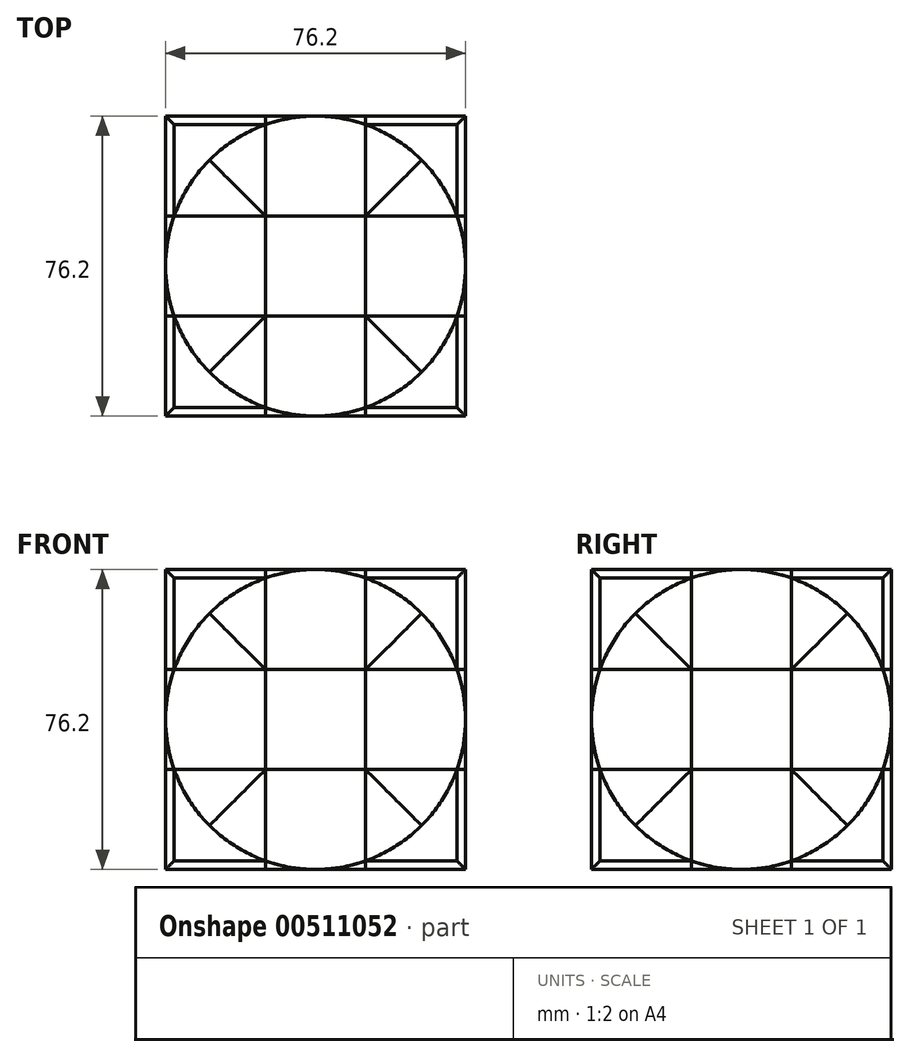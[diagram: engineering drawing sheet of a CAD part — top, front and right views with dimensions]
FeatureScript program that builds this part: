
annotation { "Feature Type Name" : "Feature", "Feature Type Description" : "" }
export const myFeature = defineFeature(function(context is Context, id is Id, definition is map)
    precondition{}
    {
        {
            var Q0;
            Q0=qCreatedBy(makeId("Front.planeOp"),FACE);
            var sketch = newSketch(context, id + "F0", { "sketchPlane" : qUnion([Q0])});
            skLineSegment(sketch, "E0.bottom", {"start": v(-38.1, 38.1) * mm, "end": v(38.1, 38.1) * mm});
            skLineSegment(sketch, "E0.top", {"start": v(-38.1, -38.1) * mm, "end": v(38.1, -38.1) * mm});
            skLineSegment(sketch, "E0.left", {"start": v(-38.1, 38.1) * mm, "end": v(-38.1, -38.1) * mm});
            skLineSegment(sketch, "E0.right", {"start": v(38.1, 38.1) * mm, "end": v(38.1, -38.1) * mm});
            skPoint(sketch, "E0.middle", {"position": v(0, 0) * mm});
            skSolve(sketch);
        }
        {
            var Q0;
            Q0=makeQuery(id+"F0.imprint","IMPRINT",FACE,{"disambiguationData":[TD([[makeQuery(id+"F0.imprint","IMPRINT",EDGE,{"derivedFrom":sQuery(id+"F0.wireOp",EDGE,"E0.bottom")}),-1.0]])]});
            extrude(context, id + "F1", {"entities" : qUnion([Q0]), "depth" : 76.2 * mm});
        }
        {
            var Q0;
            Q0=makeQuery(id+"F1.opExtrude","CAP_FACE",FACE,{"disambiguationData":[OSD([sQuery(id+"F0.wireOp",EDGE,"E0.bottom"),sQuery(id+"F0.wireOp",EDGE,"E0.top"),sQuery(id+"F0.wireOp",EDGE,"E0.left"),sQuery(id+"F0.wireOp",EDGE,"E0.right")])],"isStart":false});
            var sketch = newSketch(context, id + "F2", { "sketchPlane" : qUnion([Q0])});
            skCircle(sketch, "E1", {"center": v(0, 0) * mm, "radius": 38.1 * mm});
            skPoint(sketch, "E1.first.point", {"position": v(0, 38.1) * mm});
            skPoint(sketch, "E1.second.point", {"position": v(-38.1, 0) * mm});
            skPoint(sketch, "E1.third.point", {"position": v(0, -38.1) * mm});
            skSolve(sketch);
        }
        {
            var Q0;
            Q0=makeQuery(id+"F1.opExtrude","SWEPT_FACE",FACE,{"disambiguationData":[OSD([sQuery(id+"F0.wireOp",EDGE,"E0.right")])]});
            var sketch = newSketch(context, id + "F3", { "sketchPlane" : qUnion([Q0])});
            skCircle(sketch, "E2", {"center": v(-38.1, 0) * mm, "radius": 38.1 * mm});
            skPoint(sketch, "E2.first.point", {"position": v(-38.1, 38.1) * mm});
            skPoint(sketch, "E2.second.point", {"position": v(-76.2, 0) * mm});
            skPoint(sketch, "E2.third.point", {"position": v(-38.1, -38.1) * mm});
            skSolve(sketch);
        }
        {
            var Q0;
            {var subQ0=sQuery(id+"F2.wireOp",EDGE,"E1");var subQ1=makeQuery(id+"F2.imprint","INTERSECT",VERTEX,{"derivedFrom":[makeQuery(id+"F1.opExtrude","CAP_EDGE",EDGE,{"disambiguationData":[OSD([sQuery(id+"F0.wireOp",EDGE,"E0.bottom")])],"isStart":false}),subQ0]});Q0=makeQuery(id+"F2.imprint","IMPRINT",FACE,{"disambiguationData":[TD([[makeQuery(id+"F2.imprint","IMPRINT",EDGE,{"disambiguationData":[TD([[subQ1,1.0]])],"derivedFrom":subQ0}),1.0]])]});}
            extrude(context, id + "F4", {"entities" : qUnion([Q0]), "operationType" : NewBodyOperationType.ADD, "oppositeDirection" : true, "depth" : 76.2 * mm, "offsetDistance" : 25.4 * mm});
        }
        {
            var Q0;
            {var subQ0=sQuery(id+"F3.wireOp",EDGE,"E2");var subQ1=sQuery(id+"F0.wireOp",EDGE,"E0.right");var subQ3=makeQuery(id+"F3.imprint","INTERSECT",VERTEX,{"derivedFrom":[makeQuery(id+"F1.opExtrude","CAP_EDGE",EDGE,{"disambiguationData":[OSD([subQ1])],"isStart":true}),subQ0]});Q0=makeQuery(id+"F3.imprint","IMPRINT",FACE,{"disambiguationData":[TD([[makeQuery(id+"F3.imprint","IMPRINT",EDGE,{"disambiguationData":[TD([[subQ3,-1.0]])],"derivedFrom":subQ0}),1.0]])]});}
            extrude(context, id + "F5", {"entities" : qUnion([Q0]), "operationType" : NewBodyOperationType.ADD, "oppositeDirection" : true, "depth" : 76.2 * mm, "offsetDistance" : 25.4 * mm});
        }
        {
            var Q0;
            Q0=makeQuery(id+"F1.opExtrude","SWEPT_FACE",FACE,{"disambiguationData":[OSD([sQuery(id+"F0.wireOp",EDGE,"E0.left")])]});
            var sketch = newSketch(context, id + "F6", { "sketchPlane" : qUnion([Q0])});
            skCircle(sketch, "E3", {"center": v(38.1, 0) * mm, "radius": 38.1 * mm});
            skPoint(sketch, "E3.first.point", {"position": v(38.1, 38.1) * mm});
            skPoint(sketch, "E3.second.point", {"position": v(0, 0) * mm});
            skPoint(sketch, "E3.third.point", {"position": v(38.1, -38.1) * mm});
            skSolve(sketch);
        }
        {
            var Q0;
            Q0=makeQuery(id+"F1.opExtrude","CAP_FACE",FACE,{"disambiguationData":[OSD([sQuery(id+"F0.wireOp",EDGE,"E0.bottom"),sQuery(id+"F0.wireOp",EDGE,"E0.top"),sQuery(id+"F0.wireOp",EDGE,"E0.left"),sQuery(id+"F0.wireOp",EDGE,"E0.right")])],"isStart":true});
            var sketch = newSketch(context, id + "F7", { "sketchPlane" : qUnion([Q0])});
            skCircle(sketch, "E4", {"center": v(0, 0) * mm, "radius": 38.1 * mm});
            skPoint(sketch, "E4.first.point", {"position": v(0, 38.1) * mm});
            skPoint(sketch, "E4.second.point", {"position": v(-38.1, 0) * mm});
            skPoint(sketch, "E4.third.point", {"position": v(0, -38.1) * mm});
            skSolve(sketch);
        }
        {
            var Q0;
            {var subQ0=sQuery(id+"F7.wireOp",EDGE,"E4");var subQ1=makeQuery(id+"F7.imprint","INTERSECT",VERTEX,{"derivedFrom":[makeQuery(id+"F1.opExtrude","CAP_EDGE",EDGE,{"disambiguationData":[OSD([sQuery(id+"F0.wireOp",EDGE,"E0.bottom")])],"isStart":true}),subQ0]});Q0=makeQuery(id+"F7.imprint","IMPRINT",FACE,{"disambiguationData":[TD([[makeQuery(id+"F7.imprint","IMPRINT",EDGE,{"disambiguationData":[TD([[subQ1,1.0]])],"derivedFrom":subQ0}),1.0]])]});}
            extrude(context, id + "F8", {"entities" : qUnion([Q0]), "operationType" : NewBodyOperationType.ADD, "oppositeDirection" : true, "depth" : 76.2 * mm, "offsetDistance" : 25.4 * mm});
        }
        {
            var Q0;
            {var subQ0=sQuery(id+"F6.wireOp",EDGE,"E3");var subQ1=sQuery(id+"F0.wireOp",EDGE,"E0.left");var subQ3=makeQuery(id+"F6.imprint","INTERSECT",VERTEX,{"derivedFrom":[makeQuery(id+"F1.opExtrude","CAP_EDGE",EDGE,{"disambiguationData":[OSD([subQ1])],"isStart":false}),subQ0]});Q0=makeQuery(id+"F6.imprint","IMPRINT",FACE,{"disambiguationData":[TD([[makeQuery(id+"F6.imprint","IMPRINT",EDGE,{"disambiguationData":[TD([[subQ3,-1.0]])],"derivedFrom":subQ0}),1.0]])]});}
            extrude(context, id + "F9", {"entities" : qUnion([Q0]), "operationType" : NewBodyOperationType.ADD, "oppositeDirection" : true, "depth" : 76.2 * mm, "offsetDistance" : 25.4 * mm});
        }
        {
            var Q0;
            Q0=makeQuery(id+"F1.opExtrude","SWEPT_FACE",FACE,{"disambiguationData":[OSD([sQuery(id+"F0.wireOp",EDGE,"E0.bottom")])]});
            var sketch = newSketch(context, id + "F10", { "sketchPlane" : qUnion([Q0])});
            skCircle(sketch, "E5", {"center": v(0, -38.1) * mm, "radius": 38.1 * mm});
            skPoint(sketch, "E5.first.point", {"position": v(0, 0) * mm});
            skPoint(sketch, "E5.second.point", {"position": v(-38.1, -38.1) * mm});
            skPoint(sketch, "E5.third.point", {"position": v(0, -76.2) * mm});
            skSolve(sketch);
        }
        {
            var Q0;
            {var subQ0=sQuery(id+"F10.wireOp",EDGE,"E5");var subQ1=sQuery(id+"F0.wireOp",EDGE,"E0.bottom");var subQ2=makeQuery(id+"F10.imprint","INTERSECT",VERTEX,{"derivedFrom":[makeQuery(id+"F1.opExtrude","CAP_EDGE",EDGE,{"disambiguationData":[OSD([subQ1])],"isStart":true}),subQ0]});Q0=makeQuery(id+"F10.imprint","IMPRINT",FACE,{"disambiguationData":[TD([[makeQuery(id+"F10.imprint","IMPRINT",EDGE,{"disambiguationData":[TD([[subQ2,1.0]])],"derivedFrom":subQ0}),1.0]])]});}
            extrude(context, id + "F11", {"entities" : qUnion([Q0]), "operationType" : NewBodyOperationType.ADD, "oppositeDirection" : true, "depth" : 76.2 * mm, "offsetDistance" : 25.4 * mm});
        }
        {
            var Q0;
            Q0=makeQuery(id+"F1.opExtrude","SWEPT_FACE",FACE,{"disambiguationData":[OSD([sQuery(id+"F0.wireOp",EDGE,"E0.top")])]});
            var sketch = newSketch(context, id + "F12", { "sketchPlane" : qUnion([Q0])});
            skCircle(sketch, "E6", {"center": v(0, 38.1) * mm, "radius": 38.1 * mm});
            skPoint(sketch, "E6.first.point", {"position": v(0, 76.2) * mm});
            skPoint(sketch, "E6.second.point", {"position": v(-38.1, 38.1) * mm});
            skPoint(sketch, "E6.third.point", {"position": v(0, 0) * mm});
            skSolve(sketch);
        }
        {
            var Q0;
            {var subQ0=sQuery(id+"F12.wireOp",EDGE,"E6");var subQ1=sQuery(id+"F0.wireOp",EDGE,"E0.top");var subQ2=makeQuery(id+"F12.imprint","INTERSECT",VERTEX,{"derivedFrom":[makeQuery(id+"F1.opExtrude","CAP_EDGE",EDGE,{"disambiguationData":[OSD([subQ1])],"isStart":false}),subQ0]});Q0=makeQuery(id+"F12.imprint","IMPRINT",FACE,{"disambiguationData":[TD([[makeQuery(id+"F12.imprint","IMPRINT",EDGE,{"disambiguationData":[TD([[subQ2,1.0]])],"derivedFrom":subQ0}),1.0]])]});}
            extrude(context, id + "F13", {"entities" : qUnion([Q0]), "operationType" : NewBodyOperationType.ADD, "oppositeDirection" : true, "depth" : 76.2 * mm, "offsetDistance" : 25.4 * mm});
        }
        {
            var Q0;
            {var subQ0=sQuery(id+"F2.wireOp",EDGE,"E1");var subQ1=makeQuery(id+"F1.opExtrude","CAP_EDGE",EDGE,{"disambiguationData":[OSD([sQuery(id+"F0.wireOp",EDGE,"E0.bottom")])],"isStart":false});var subQ2=makeQuery(id+"F2.imprint","INTERSECT",VERTEX,{"derivedFrom":[subQ1,subQ0]});Q0=makeQuery(id+"F2.imprint","IMPRINT",FACE,{"disambiguationData":[TD([[makeQuery(id+"F2.imprint","IMPRINT",EDGE,{"disambiguationData":[TD([[subQ2,1.0]])],"derivedFrom":subQ0}),-1.0]])]});}
            extrude(context, id + "F14", {"entities" : qUnion([Q0]), "operationType" : NewBodyOperationType.REMOVE, "oppositeDirection" : true, "depth" : 25.4 * mm, "offsetDistance" : 25.4 * mm});
        }
        {
            var Q0;
            {var subQ0=sQuery(id+"F2.wireOp",EDGE,"E1");var subQ1=makeQuery(id+"F1.opExtrude","CAP_EDGE",EDGE,{"disambiguationData":[OSD([sQuery(id+"F0.wireOp",EDGE,"E0.bottom")])],"isStart":false});var subQ2=makeQuery(id+"F2.imprint","INTERSECT",VERTEX,{"derivedFrom":[subQ1,subQ0]});Q0=makeQuery(id+"F2.imprint","IMPRINT",FACE,{"disambiguationData":[TD([[makeQuery(id+"F2.imprint","IMPRINT",EDGE,{"disambiguationData":[TD([[subQ2,-1.0]])],"derivedFrom":subQ0}),-1.0]])]});}
            extrude(context, id + "F15", {"entities" : qUnion([Q0]), "operationType" : NewBodyOperationType.REMOVE, "oppositeDirection" : true, "depth" : 25.4 * mm, "offsetDistance" : 25.4 * mm});
        }
        {
            var Q0;
            {var subQ0=sQuery(id+"F2.wireOp",EDGE,"E1");var subQ1=makeQuery(id+"F1.opExtrude","CAP_EDGE",EDGE,{"disambiguationData":[OSD([sQuery(id+"F0.wireOp",EDGE,"E0.right")])],"isStart":false});var subQ2=makeQuery(id+"F2.imprint","INTERSECT",VERTEX,{"derivedFrom":[subQ1,subQ0]});Q0=makeQuery(id+"F2.imprint","IMPRINT",FACE,{"disambiguationData":[TD([[makeQuery(id+"F2.imprint","IMPRINT",EDGE,{"disambiguationData":[TD([[subQ2,1.0]])],"derivedFrom":subQ0}),-1.0]])]});}
            var Q1;
            {var subQ0=sQuery(id+"F2.wireOp",EDGE,"E1");var subQ1=makeQuery(id+"F1.opExtrude","CAP_EDGE",EDGE,{"disambiguationData":[OSD([sQuery(id+"F0.wireOp",EDGE,"E0.left")])],"isStart":false});var subQ2=makeQuery(id+"F2.imprint","INTERSECT",VERTEX,{"derivedFrom":[subQ1,subQ0]});Q1=makeQuery(id+"F2.imprint","IMPRINT",FACE,{"disambiguationData":[TD([[makeQuery(id+"F2.imprint","IMPRINT",EDGE,{"disambiguationData":[TD([[subQ2,-1.0]])],"derivedFrom":subQ0}),-1.0]])]});}
            extrude(context, id + "F16", {"entities" : qUnion([Q0, Q1]), "operationType" : NewBodyOperationType.REMOVE, "oppositeDirection" : true, "depth" : 25.4 * mm, "offsetDistance" : 25.4 * mm});
        }
        {
            var Q0;
            {var subQ0=sQuery(id+"F3.wireOp",EDGE,"E2");var subQ1=sQuery(id+"F0.wireOp",EDGE,"E0.right");var subQ4=makeQuery(id+"F1.opExtrude","CAP_EDGE",EDGE,{"disambiguationData":[OSD([subQ1])],"isStart":false});var subQ5=makeQuery(id+"F3.imprint","INTERSECT",VERTEX,{"derivedFrom":[subQ4,subQ0]});Q0=makeQuery(id+"F3.imprint","IMPRINT",FACE,{"disambiguationData":[TD([[makeQuery(id+"F3.imprint","IMPRINT",EDGE,{"disambiguationData":[TD([[subQ5,1.0]])],"derivedFrom":subQ0}),-1.0]])]});}
            extrude(context, id + "F17", {"entities" : qUnion([Q0]), "operationType" : NewBodyOperationType.REMOVE, "oppositeDirection" : true, "depth" : 25.4 * mm, "offsetDistance" : 25.4 * mm});
        }
        {
            var Q0;
            {var subQ0=sQuery(id+"F3.wireOp",EDGE,"E2");var subQ1=sQuery(id+"F0.wireOp",EDGE,"E0.right");var subQ4=makeQuery(id+"F1.opExtrude","CAP_EDGE",EDGE,{"disambiguationData":[OSD([subQ1])],"isStart":true});var subQ5=makeQuery(id+"F3.imprint","INTERSECT",VERTEX,{"derivedFrom":[subQ4,subQ0]});Q0=makeQuery(id+"F3.imprint","IMPRINT",FACE,{"disambiguationData":[TD([[makeQuery(id+"F3.imprint","IMPRINT",EDGE,{"disambiguationData":[TD([[subQ5,-1.0]])],"derivedFrom":subQ0}),-1.0]])]});}
            var Q1;
            {var subQ0=sQuery(id+"F3.wireOp",EDGE,"E2");var subQ1=sQuery(id+"F0.wireOp",EDGE,"E0.right");var subQ2=makeQuery(id+"F1.opExtrude","CAP_EDGE",EDGE,{"disambiguationData":[OSD([subQ1])],"isStart":true});var subQ3=makeQuery(id+"F3.imprint","INTERSECT",VERTEX,{"derivedFrom":[subQ2,subQ0]});Q1=makeQuery(id+"F3.imprint","IMPRINT",FACE,{"disambiguationData":[TD([[makeQuery(id+"F3.imprint","IMPRINT",EDGE,{"disambiguationData":[TD([[subQ3,1.0]])],"derivedFrom":subQ0}),-1.0]])]});}
            var Q2;
            {var subQ0=sQuery(id+"F3.wireOp",EDGE,"E2");var subQ1=sQuery(id+"F0.wireOp",EDGE,"E0.right");var subQ2=makeQuery(id+"F1.opExtrude","CAP_EDGE",EDGE,{"disambiguationData":[OSD([subQ1])],"isStart":false});var subQ3=makeQuery(id+"F3.imprint","INTERSECT",VERTEX,{"derivedFrom":[subQ2,subQ0]});Q2=makeQuery(id+"F3.imprint","IMPRINT",FACE,{"disambiguationData":[TD([[makeQuery(id+"F3.imprint","IMPRINT",EDGE,{"disambiguationData":[TD([[subQ3,-1.0]])],"derivedFrom":subQ0}),-1.0]])]});}
            var Q3;
            {var subQ0=sQuery(id+"F3.wireOp",EDGE,"E2");var subQ1=sQuery(id+"F0.wireOp",EDGE,"E0.right");var subQ4=makeQuery(id+"F1.opExtrude","CAP_EDGE",EDGE,{"disambiguationData":[OSD([subQ1])],"isStart":false});var subQ5=makeQuery(id+"F3.imprint","INTERSECT",VERTEX,{"derivedFrom":[subQ4,subQ0]});Q3=makeQuery(id+"F3.imprint","IMPRINT",FACE,{"disambiguationData":[TD([[makeQuery(id+"F3.imprint","IMPRINT",EDGE,{"disambiguationData":[TD([[subQ5,1.0]])],"derivedFrom":subQ0}),-1.0]])]});}
            extrude(context, id + "F18", {"entities" : qUnion([Q0, Q1, Q2, Q3]), "operationType" : NewBodyOperationType.REMOVE, "oppositeDirection" : true, "depth" : 25.4 * mm, "offsetDistance" : 25.4 * mm});
        }
        {
            var Q0;
            {var subQ0=sQuery(id+"F6.wireOp",EDGE,"E3");var subQ1=sQuery(id+"F0.wireOp",EDGE,"E0.left");var subQ4=makeQuery(id+"F1.opExtrude","CAP_EDGE",EDGE,{"disambiguationData":[OSD([subQ1])],"isStart":true});var subQ5=makeQuery(id+"F6.imprint","INTERSECT",VERTEX,{"derivedFrom":[subQ4,subQ0]});Q0=makeQuery(id+"F6.imprint","IMPRINT",FACE,{"disambiguationData":[TD([[makeQuery(id+"F6.imprint","IMPRINT",EDGE,{"disambiguationData":[TD([[subQ5,1.0]])],"derivedFrom":subQ0}),-1.0]])]});}
            var Q1;
            {var subQ0=sQuery(id+"F6.wireOp",EDGE,"E3");var subQ1=sQuery(id+"F0.wireOp",EDGE,"E0.left");var subQ4=makeQuery(id+"F1.opExtrude","CAP_EDGE",EDGE,{"disambiguationData":[OSD([subQ1])],"isStart":false});var subQ5=makeQuery(id+"F6.imprint","INTERSECT",VERTEX,{"derivedFrom":[subQ4,subQ0]});Q1=makeQuery(id+"F6.imprint","IMPRINT",FACE,{"disambiguationData":[TD([[makeQuery(id+"F6.imprint","IMPRINT",EDGE,{"disambiguationData":[TD([[subQ5,-1.0]])],"derivedFrom":subQ0}),-1.0]])]});}
            var Q2;
            {var subQ0=sQuery(id+"F6.wireOp",EDGE,"E3");var subQ1=sQuery(id+"F0.wireOp",EDGE,"E0.left");var subQ2=makeQuery(id+"F1.opExtrude","CAP_EDGE",EDGE,{"disambiguationData":[OSD([subQ1])],"isStart":false});var subQ3=makeQuery(id+"F6.imprint","INTERSECT",VERTEX,{"derivedFrom":[subQ2,subQ0]});Q2=makeQuery(id+"F6.imprint","IMPRINT",FACE,{"disambiguationData":[TD([[makeQuery(id+"F6.imprint","IMPRINT",EDGE,{"disambiguationData":[TD([[subQ3,1.0]])],"derivedFrom":subQ0}),-1.0]])]});}
            var Q3;
            {var subQ0=sQuery(id+"F6.wireOp",EDGE,"E3");var subQ1=sQuery(id+"F0.wireOp",EDGE,"E0.left");var subQ2=makeQuery(id+"F1.opExtrude","CAP_EDGE",EDGE,{"disambiguationData":[OSD([subQ1])],"isStart":true});var subQ3=makeQuery(id+"F6.imprint","INTERSECT",VERTEX,{"derivedFrom":[subQ2,subQ0]});Q3=makeQuery(id+"F6.imprint","IMPRINT",FACE,{"disambiguationData":[TD([[makeQuery(id+"F6.imprint","IMPRINT",EDGE,{"disambiguationData":[TD([[subQ3,-1.0]])],"derivedFrom":subQ0}),-1.0]])]});}
            extrude(context, id + "F19", {"entities" : qUnion([Q0, Q1, Q2, Q3]), "operationType" : NewBodyOperationType.REMOVE, "oppositeDirection" : true, "depth" : 25.4 * mm, "offsetDistance" : 25.4 * mm});
        }
        {
            var Q0;
            {var subQ0=sQuery(id+"F7.wireOp",EDGE,"E4");var subQ1=makeQuery(id+"F1.opExtrude","CAP_EDGE",EDGE,{"disambiguationData":[OSD([sQuery(id+"F0.wireOp",EDGE,"E0.bottom")])],"isStart":true});var subQ2=makeQuery(id+"F7.imprint","INTERSECT",VERTEX,{"derivedFrom":[subQ1,subQ0]});Q0=makeQuery(id+"F7.imprint","IMPRINT",FACE,{"disambiguationData":[TD([[makeQuery(id+"F7.imprint","IMPRINT",EDGE,{"disambiguationData":[TD([[subQ2,-1.0]])],"derivedFrom":subQ0}),-1.0]])]});}
            var Q1;
            {var subQ0=sQuery(id+"F7.wireOp",EDGE,"E4");var subQ1=makeQuery(id+"F1.opExtrude","CAP_EDGE",EDGE,{"disambiguationData":[OSD([sQuery(id+"F0.wireOp",EDGE,"E0.bottom")])],"isStart":true});var subQ2=makeQuery(id+"F7.imprint","INTERSECT",VERTEX,{"derivedFrom":[subQ1,subQ0]});Q1=makeQuery(id+"F7.imprint","IMPRINT",FACE,{"disambiguationData":[TD([[makeQuery(id+"F7.imprint","IMPRINT",EDGE,{"disambiguationData":[TD([[subQ2,1.0]])],"derivedFrom":subQ0}),-1.0]])]});}
            var Q2;
            {var subQ0=sQuery(id+"F7.wireOp",EDGE,"E4");var subQ1=makeQuery(id+"F1.opExtrude","CAP_EDGE",EDGE,{"disambiguationData":[OSD([sQuery(id+"F0.wireOp",EDGE,"E0.left")])],"isStart":true});var subQ2=makeQuery(id+"F7.imprint","INTERSECT",VERTEX,{"derivedFrom":[subQ1,subQ0]});Q2=makeQuery(id+"F7.imprint","IMPRINT",FACE,{"disambiguationData":[TD([[makeQuery(id+"F7.imprint","IMPRINT",EDGE,{"disambiguationData":[TD([[subQ2,1.0]])],"derivedFrom":subQ0}),-1.0]])]});}
            var Q3;
            {var subQ0=sQuery(id+"F7.wireOp",EDGE,"E4");var subQ1=makeQuery(id+"F1.opExtrude","CAP_EDGE",EDGE,{"disambiguationData":[OSD([sQuery(id+"F0.wireOp",EDGE,"E0.right")])],"isStart":true});var subQ2=makeQuery(id+"F7.imprint","INTERSECT",VERTEX,{"derivedFrom":[subQ1,subQ0]});Q3=makeQuery(id+"F7.imprint","IMPRINT",FACE,{"disambiguationData":[TD([[makeQuery(id+"F7.imprint","IMPRINT",EDGE,{"disambiguationData":[TD([[subQ2,-1.0]])],"derivedFrom":subQ0}),-1.0]])]});}
            extrude(context, id + "F20", {"entities" : qUnion([Q0, Q1, Q2, Q3]), "operationType" : NewBodyOperationType.REMOVE, "oppositeDirection" : true, "depth" : 25.4 * mm, "offsetDistance" : 25.4 * mm});
        }
        {
            var Q0;
            {var subQ0=sQuery(id+"F10.wireOp",EDGE,"E5");var subQ1=sQuery(id+"F0.wireOp",EDGE,"E0.bottom");var subQ2=makeQuery(id+"F1.opExtrude","CAP_EDGE",EDGE,{"disambiguationData":[OSD([subQ1])],"isStart":true});var subQ3=makeQuery(id+"F10.imprint","INTERSECT",VERTEX,{"derivedFrom":[subQ2,subQ0]});Q0=makeQuery(id+"F10.imprint","IMPRINT",FACE,{"disambiguationData":[TD([[makeQuery(id+"F10.imprint","IMPRINT",EDGE,{"disambiguationData":[TD([[subQ3,1.0]])],"derivedFrom":subQ0}),-1.0]])]});}
            var Q1;
            {var subQ0=sQuery(id+"F10.wireOp",EDGE,"E5");var subQ1=sQuery(id+"F0.wireOp",EDGE,"E0.bottom");var subQ4=makeQuery(id+"F1.opExtrude","CAP_EDGE",EDGE,{"disambiguationData":[OSD([subQ1])],"isStart":false});var subQ5=makeQuery(id+"F10.imprint","INTERSECT",VERTEX,{"derivedFrom":[subQ4,subQ0]});Q1=makeQuery(id+"F10.imprint","IMPRINT",FACE,{"disambiguationData":[TD([[makeQuery(id+"F10.imprint","IMPRINT",EDGE,{"disambiguationData":[TD([[subQ5,-1.0]])],"derivedFrom":subQ0}),-1.0]])]});}
            var Q2;
            {var subQ0=sQuery(id+"F10.wireOp",EDGE,"E5");var subQ1=sQuery(id+"F0.wireOp",EDGE,"E0.bottom");var subQ4=makeQuery(id+"F1.opExtrude","CAP_EDGE",EDGE,{"disambiguationData":[OSD([subQ1])],"isStart":false});var subQ5=makeQuery(id+"F10.imprint","INTERSECT",VERTEX,{"derivedFrom":[subQ4,subQ0]});Q2=makeQuery(id+"F10.imprint","IMPRINT",FACE,{"disambiguationData":[TD([[makeQuery(id+"F10.imprint","IMPRINT",EDGE,{"disambiguationData":[TD([[subQ5,1.0]])],"derivedFrom":subQ0}),-1.0]])]});}
            var Q3;
            {var subQ0=sQuery(id+"F10.wireOp",EDGE,"E5");var subQ1=sQuery(id+"F0.wireOp",EDGE,"E0.bottom");var subQ2=makeQuery(id+"F1.opExtrude","CAP_EDGE",EDGE,{"disambiguationData":[OSD([subQ1])],"isStart":true});var subQ3=makeQuery(id+"F10.imprint","INTERSECT",VERTEX,{"derivedFrom":[subQ2,subQ0]});Q3=makeQuery(id+"F10.imprint","IMPRINT",FACE,{"disambiguationData":[TD([[makeQuery(id+"F10.imprint","IMPRINT",EDGE,{"disambiguationData":[TD([[subQ3,-1.0]])],"derivedFrom":subQ0}),-1.0]])]});}
            extrude(context, id + "F21", {"entities" : qUnion([Q0, Q1, Q2, Q3]), "operationType" : NewBodyOperationType.REMOVE, "oppositeDirection" : true, "depth" : 25.4 * mm, "offsetDistance" : 25.4 * mm});
        }
        {
            var Q0;
            {var subQ0=sQuery(id+"F12.wireOp",EDGE,"E6");var subQ1=sQuery(id+"F0.wireOp",EDGE,"E0.top");var subQ4=makeQuery(id+"F1.opExtrude","CAP_EDGE",EDGE,{"disambiguationData":[OSD([subQ1])],"isStart":true});var subQ5=makeQuery(id+"F12.imprint","INTERSECT",VERTEX,{"derivedFrom":[subQ4,subQ0]});Q0=makeQuery(id+"F12.imprint","IMPRINT",FACE,{"disambiguationData":[TD([[makeQuery(id+"F12.imprint","IMPRINT",EDGE,{"disambiguationData":[TD([[subQ5,1.0]])],"derivedFrom":subQ0}),-1.0]])]});}
            var Q1;
            {var subQ0=sQuery(id+"F12.wireOp",EDGE,"E6");var subQ1=sQuery(id+"F0.wireOp",EDGE,"E0.top");var subQ2=makeQuery(id+"F1.opExtrude","CAP_EDGE",EDGE,{"disambiguationData":[OSD([subQ1])],"isStart":false});var subQ3=makeQuery(id+"F12.imprint","INTERSECT",VERTEX,{"derivedFrom":[subQ2,subQ0]});Q1=makeQuery(id+"F12.imprint","IMPRINT",FACE,{"disambiguationData":[TD([[makeQuery(id+"F12.imprint","IMPRINT",EDGE,{"disambiguationData":[TD([[subQ3,-1.0]])],"derivedFrom":subQ0}),-1.0]])]});}
            var Q2;
            {var subQ0=sQuery(id+"F12.wireOp",EDGE,"E6");var subQ1=sQuery(id+"F0.wireOp",EDGE,"E0.top");var subQ2=makeQuery(id+"F1.opExtrude","CAP_EDGE",EDGE,{"disambiguationData":[OSD([subQ1])],"isStart":false});var subQ3=makeQuery(id+"F12.imprint","INTERSECT",VERTEX,{"derivedFrom":[subQ2,subQ0]});Q2=makeQuery(id+"F12.imprint","IMPRINT",FACE,{"disambiguationData":[TD([[makeQuery(id+"F12.imprint","IMPRINT",EDGE,{"disambiguationData":[TD([[subQ3,1.0]])],"derivedFrom":subQ0}),-1.0]])]});}
            var Q3;
            {var subQ0=sQuery(id+"F12.wireOp",EDGE,"E6");var subQ1=sQuery(id+"F0.wireOp",EDGE,"E0.top");var subQ4=makeQuery(id+"F1.opExtrude","CAP_EDGE",EDGE,{"disambiguationData":[OSD([subQ1])],"isStart":true});var subQ5=makeQuery(id+"F12.imprint","INTERSECT",VERTEX,{"derivedFrom":[subQ4,subQ0]});Q3=makeQuery(id+"F12.imprint","IMPRINT",FACE,{"disambiguationData":[TD([[makeQuery(id+"F12.imprint","IMPRINT",EDGE,{"disambiguationData":[TD([[subQ5,-1.0]])],"derivedFrom":subQ0}),-1.0]])]});}
            extrude(context, id + "F22", {"entities" : qUnion([Q0, Q1, Q2, Q3]), "operationType" : NewBodyOperationType.REMOVE, "oppositeDirection" : true, "depth" : 25.4 * mm, "offsetDistance" : 25.4 * mm});
        }
    });
